# Revit family: Toilet-Floor_Mount-KOHLER-VEIL-K-1666T_1
name_source: partatom
category: Plumbing Fixtures
revit_build: Autodesk Revit 2017 (Build: 20160225_1515(x64)
units: mm (PartAtom-declared; Revit-internal decimal feet)

## family parameters
Cut with Voids When Loaded = No
Host = Face
OmniClass Number = 23.31.19.00
OmniClass Title = Toilets
Part Type = Normal
Room Calculation Point = No
Round Connector Dimension = Use Diameter
Shared = No

## types (2) — shared parameters
ADA Compliant = No
Assembly Code = D2010100
CW Connection = Yes
Cold Water Inlet = Cold Water Inlet
Date Modified = 06/22/2021
Default Elevation = 0"
Description = Class Five 2 PC Toilet 305MM
Finish = Kohler-Vitreous_China-0-White
Flow Rate = 0 GPM
Flush Rate- GPF = 0 GPF
Flush Rate- LPF = 0 LPF
HW Connection = No
Height = 29 1/2"
Hot Water Inlet = Hot Water Inlet
Length = 28 5/16"
Manufacturer = KOHLER Co.
Master Format 2014 = 22 42 13.13
Master Format 2014 Name = Residential Water Closets
Material = Vitreous China
Pressure = 0.00 psi
Product Name = VEIL
Rough-In = 12"
Seat Included = Yes
URL = http://www.kohler.com.cn
Vent Connection = No
Waste Connection = Yes
Waste Water Outlet = Waste Water Outlet
WaterSense Certified = No
Width = 15 3/16"

## per-type parameters (varying)
| type | Model | S | SL | Type |
| S, 0-White | K-1666T-S-0 | Yes | No | 1 |
| SL, 0-White | K-1666T-SL-0 | No | Yes | 2 |

## geometry (parser evidence)
native form markers: Sweep x4
no freeform markers — native parametric forms only
